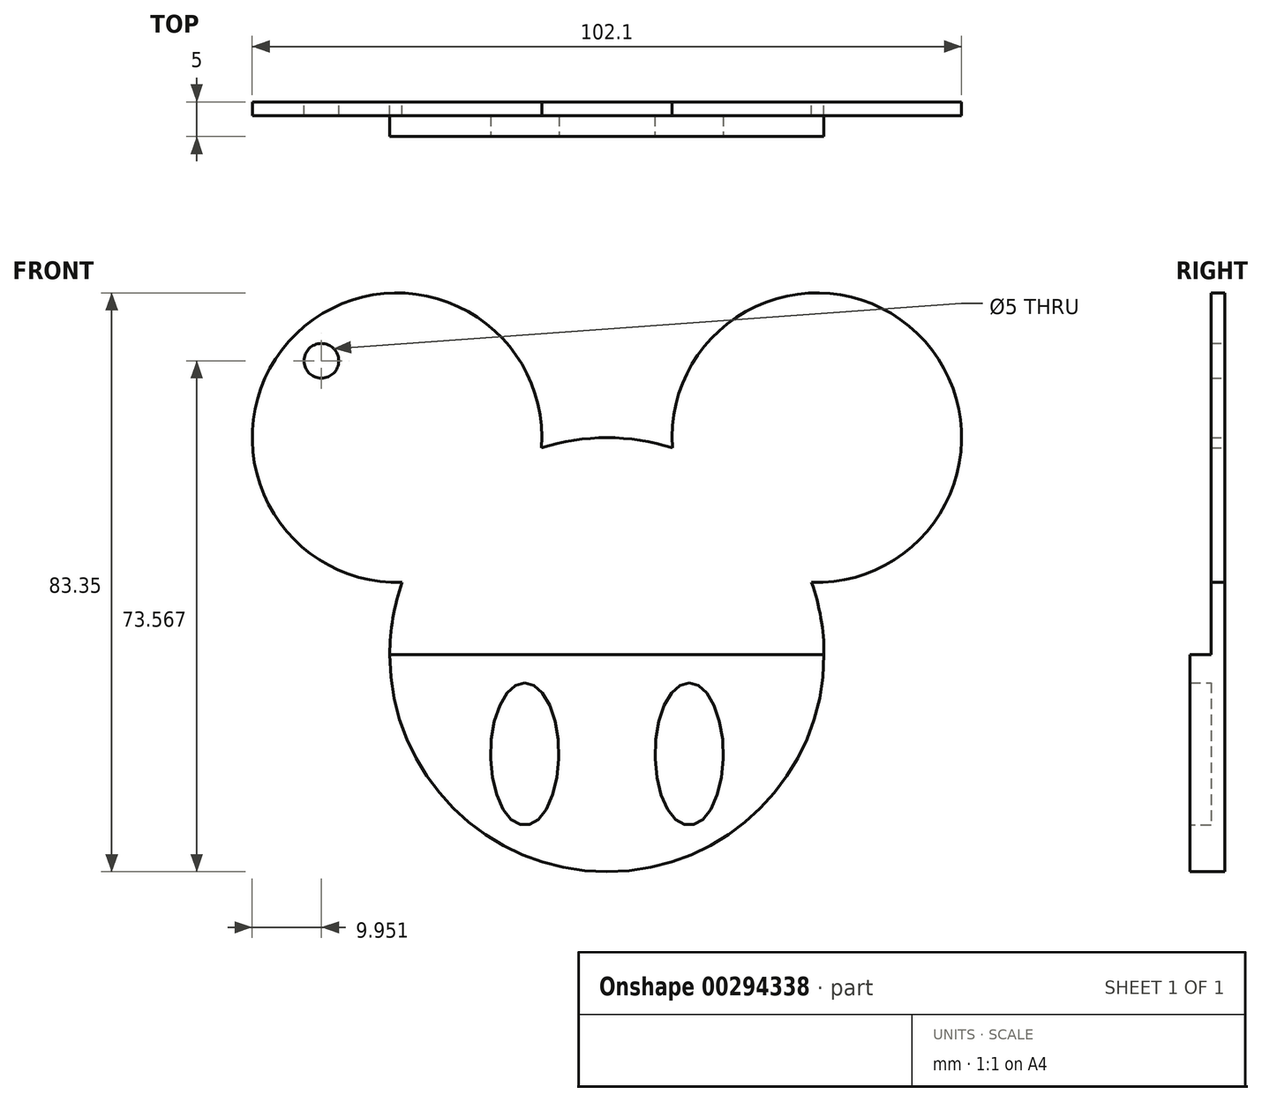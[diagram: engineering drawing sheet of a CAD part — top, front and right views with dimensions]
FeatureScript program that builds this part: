
annotation { "Feature Type Name" : "Feature", "Feature Type Description" : "" }
export const myFeature = defineFeature(function(context is Context, id is Id, definition is map)
    precondition{}
    {
        {
            var Q0;
            Q0=qCreatedBy(makeId("Front.planeOp"),FACE);
            var sketch = newSketch(context, id + "F0", { "sketchPlane" : qUnion([Q0])});
            skLineSegment(sketch, "E0", {"start": v(-36.5, 52.08) * mm, "end": v(-35.07, 52.08) * mm, "construction": true});
            skPoint(sketch, "E1.start.orphan", {"position": v(-61.6, -31.25) * mm});
            skPoint(sketch, "E2.orphan", {"position": v(-61.6, 0) * mm});
            skLineSegment(sketch, "E3", {"start": v(-5.58, -31.25) * mm, "end": v(-5.58, 31.25) * mm, "construction": true});
            skArc(sketch, "E4", {"start": v(-35.04, 10.42) * mm, "mid": v(-5.58, -31.25) * mm, "end": v(23.88, 10.42) * mm});
            skPoint(sketch, "E5.start.orphan", {"position": v(-47.25, 61.6) * mm});
            skArc(sketch, "E6", {"start": v(-14.99, 29.8) * mm, "mid": v(-50.27, 46.24) * mm, "end": v(-35.04, 10.42) * mm});
            skArc(sketch, "E7.MirrorC", {"start": v(3.83, 29.8) * mm, "mid": v(39.1, 46.24) * mm, "end": v(23.88, 10.42) * mm});
            skArc(sketch, "E8.trimOffspring", {"start": v(3.83, 29.8) * mm, "mid": v(-5.58, 31.25) * mm, "end": v(-14.99, 29.8) * mm});
            skPoint(sketch, "E9.trimOffspring.end.orphan", {"position": v(-47.25, 52.08) * mm});
            skPoint(sketch, "E10.orphan", {"position": v(36.09, 52.08) * mm});
            skPoint(sketch, "E11.orphan", {"position": v(36.09, -31.25) * mm});
            skPoint(sketch, "E12.orphan", {"position": v(-47.25, -31.25) * mm});
            skLineSegment(sketch, "E13", {"start": v(-36.83, 0) * mm, "end": v(25.67, 0) * mm});
            skPoint(sketch, "E14.start.orphan", {"position": v(-47.25, 0) * mm});
            skPoint(sketch, "E15.trimOffspring.end.orphan", {"position": v(36.09, 0) * mm});
            skPoint(sketch, "E16.start.orphan", {"position": v(-20.68, -8.04) * mm});
            skEllipse(sketch, "E17", {"center": v(-17.41, -14.29) * mm, "majorRadius": 10.27 * mm, "minorRadius": 4.92 * mm, "majorAxis": v(0, 1)});
            skEllipse(sketch, "E18.MirrorC", {"center": v(6.25, -14.29) * mm, "majorRadius": 10.27 * mm, "minorRadius": 4.92 * mm, "majorAxis": v(0, 1)});
            skCircle(sketch, "E19", {"center": v(-46.68, 42.32) * mm, "radius": 2.5 * mm});
            skPoint(sketch, "E20.orphan", {"position": v(-5.58, 52.08) * mm});
            skLineSegment(sketch, "E21", {"start": v(-47.25, -31.25) * mm, "end": v(36.09, -31.25) * mm, "construction": true});
            skLineSegment(sketch, "E22", {"start": v(36.09, 52.08) * mm, "end": v(36.09, -31.25) * mm, "construction": true});
            skLineSegment(sketch, "E23", {"start": v(36.09, 52.08) * mm, "end": v(-47.25, 52.08) * mm, "construction": true});
            skLineSegment(sketch, "E24", {"start": v(-47.25, -31.25) * mm, "end": v(-47.25, 52.08) * mm, "construction": true});
            skSolve(sketch);
        }
        {
            var Q0;
            {var subQ1=sQuery(id+"F0.wireOp",EDGE,"E6");Q0=makeQuery(id+"F0.imprint","IMPRINT",FACE,{"disambiguationData":[TD([[makeQuery(id+"F0.imprint","IMPRINT",EDGE,{"derivedFrom":subQ1}),1.0]])]});}
            var Q1;
            {var subQ0=sQuery(id+"F0.wireOp",EDGE,"E13");Q1=makeQuery(id+"F0.imprint","IMPRINT",FACE,{"disambiguationData":[TD([[makeQuery(id+"F0.imprint","IMPRINT",EDGE,{"derivedFrom":subQ0}),-1.0]])]});}
            var Q2;
            Q2=makeQuery(id+"F0.imprint","IMPRINT",FACE,{"disambiguationData":[TD([[makeQuery(id+"F0.imprint","IMPRINT",EDGE,{"derivedFrom":sQuery(id+"F0.wireOp",EDGE,"E17")}),1.0]])]});
            var Q3;
            Q3=makeQuery(id+"F0.imprint","IMPRINT",FACE,{"disambiguationData":[TD([[makeQuery(id+"F0.imprint","IMPRINT",EDGE,{"derivedFrom":sQuery(id+"F0.wireOp",EDGE,"E18.MirrorC")}),1.0]])]});
            extrude(context, id + "F1", {"entities" : qUnion([Q0, Q1, Q2, Q3]), "depth" : 2 * mm});
        }
        {
            var Q0;
            {var subQ0=sQuery(id+"F0.wireOp",EDGE,"E13");Q0=makeQuery(id+"F0.imprint","IMPRINT",FACE,{"disambiguationData":[TD([[makeQuery(id+"F0.imprint","IMPRINT",EDGE,{"derivedFrom":subQ0}),-1.0]])]});}
            extrude(context, id + "F2", {"entities" : qUnion([Q0]), "operationType" : NewBodyOperationType.ADD, "depth" : 5 * mm});
        }
    });
